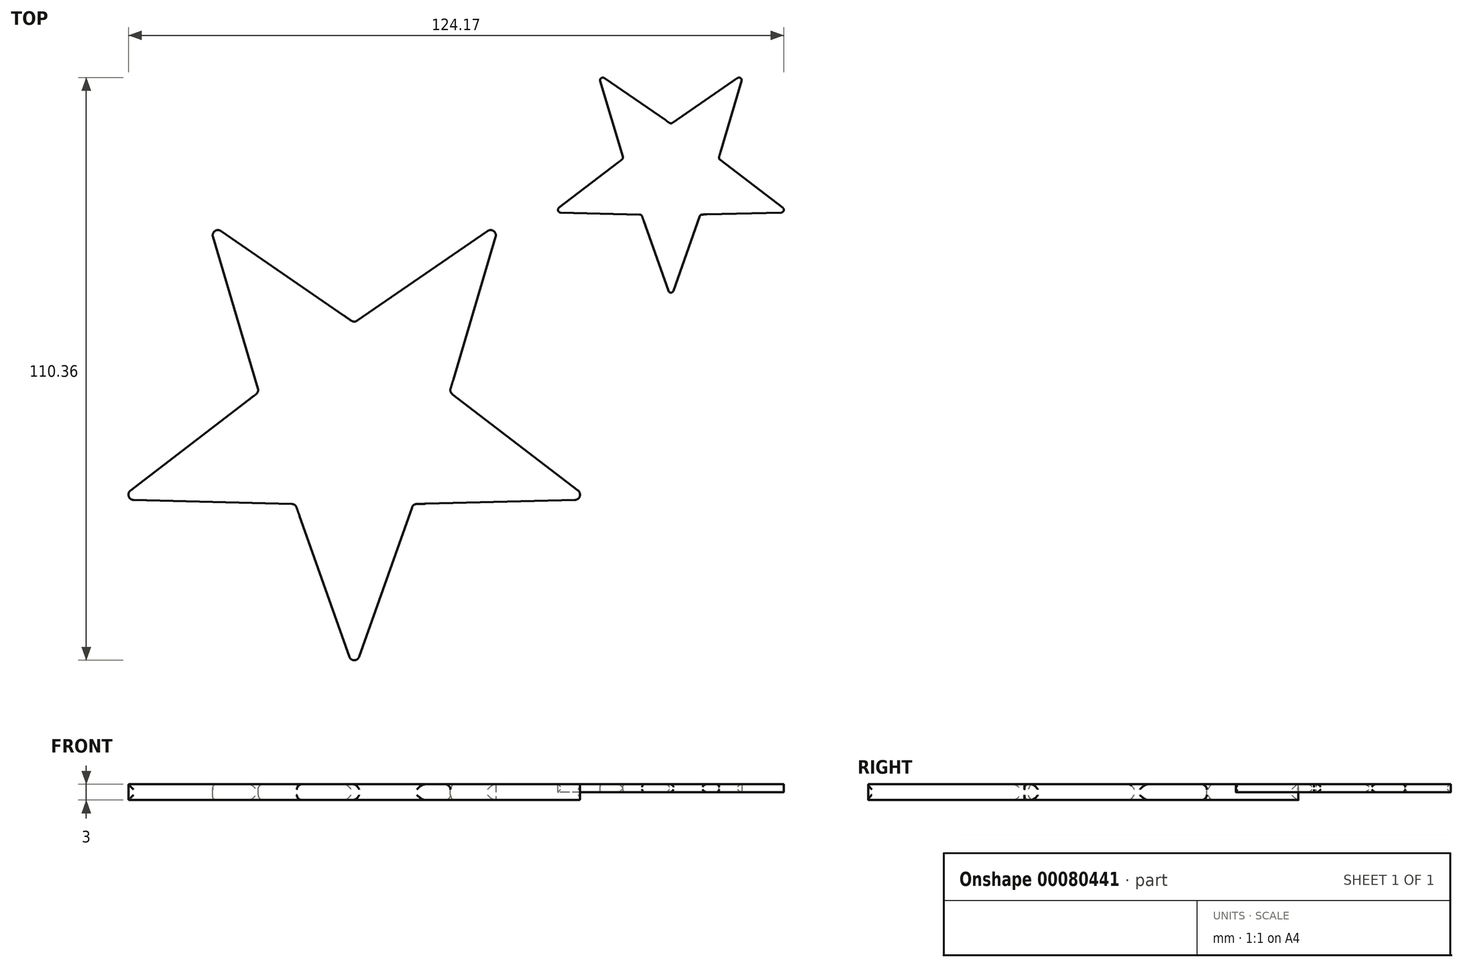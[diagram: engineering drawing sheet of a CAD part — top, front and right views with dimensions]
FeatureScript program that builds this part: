
annotation { "Feature Type Name" : "Feature", "Feature Type Description" : "" }
export const myFeature = defineFeature(function(context is Context, id is Id, definition is map)
    precondition{}
    {
        {
            var Q0;
            Q0=qCreatedBy(makeId("Top.planeOp"),FACE);
            var sketch = newSketch(context, id + "F0", { "sketchPlane" : qUnion([Q0])});
            skPoint(sketch, "E0.0.midPoint", {"position": v(0, -30.72) * mm});
            skPoint(sketch, "E1.0.midPoint", {"position": v(22.32, -30.72) * mm});
            skLineSegment(sketch, "E2", {"start": v(-27.59, 37.97) * mm, "end": v(-18.06, 5.87) * mm});
            skLineSegment(sketch, "E3", {"start": v(-18.06, 5.87) * mm, "end": v(-44.64, -14.5) * mm});
            skLineSegment(sketch, "E4", {"start": v(-27.59, 37.97) * mm, "end": v(0, 18.99) * mm});
            skLineSegment(sketch, "E5", {"start": v(0, 18.99) * mm, "end": v(27.59, 37.97) * mm});
            skLineSegment(sketch, "E6", {"start": v(27.59, 37.97) * mm, "end": v(18.06, 5.87) * mm});
            skLineSegment(sketch, "E7", {"start": v(18.06, 5.87) * mm, "end": v(44.64, -14.5) * mm});
            skLineSegment(sketch, "E8", {"start": v(44.64, -14.5) * mm, "end": v(11.16, -15.36) * mm});
            skLineSegment(sketch, "E9", {"start": v(11.16, -15.36) * mm, "end": v(0, -46.94) * mm});
            skLineSegment(sketch, "E10", {"start": v(-11.16, -15.36) * mm, "end": v(-44.64, -14.5) * mm});
            skLineSegment(sketch, "E11", {"start": v(-11.16, -15.36) * mm, "end": v(0, -46.94) * mm});
            skSolve(sketch);
        }
        {
            var Q0;
            Q0 = qSketchRegion(id + "F0", true);
            extrude(context, id + "F1", {"entities" : qUnion([Q0]), "depth" : 3 * mm});
        }
        {
            var Q0;
            Q0=makeQuery(id+"F1.opExtrude","SWEPT_FACE",FACE,{"disambiguationData":[OSD([sQuery(id+"F0.wireOp",EDGE,"E10")])]});
            var Q1;
            Q1=makeQuery(id+"F1.opExtrude","SWEPT_FACE",FACE,{"disambiguationData":[OSD([sQuery(id+"F0.wireOp",EDGE,"E9")])]});
            var Q2;
            Q2=makeQuery(id+"F1.opExtrude","SWEPT_FACE",FACE,{"disambiguationData":[OSD([sQuery(id+"F0.wireOp",EDGE,"E7")])]});
            var Q3;
            Q3=makeQuery(id+"F1.opExtrude","SWEPT_FACE",FACE,{"disambiguationData":[OSD([sQuery(id+"F0.wireOp",EDGE,"E5")])]});
            var Q4;
            Q4=makeQuery(id+"F1.opExtrude","SWEPT_FACE",FACE,{"disambiguationData":[OSD([sQuery(id+"F0.wireOp",EDGE,"E2")])]});
            fillet(context, id + "F2", {"entities" : qUnion([Q0, Q1, Q2, Q3, Q4]), "radius" : 1 * mm, "tangentPropagation" : true, "allowEdgeOverflow" : false});
        }
        {
            var Q0;
            Q0=makeQuery(id+"F1.opExtrude","SWEPT_BODY",BODY,{"disambiguationData":[OSD([sQuery(id+"F0.wireOp",EDGE,"E2"),sQuery(id+"F0.wireOp",EDGE,"E3"),sQuery(id+"F0.wireOp",EDGE,"E4"),sQuery(id+"F0.wireOp",EDGE,"E5"),sQuery(id+"F0.wireOp",EDGE,"E6"),sQuery(id+"F0.wireOp",EDGE,"E7"),sQuery(id+"F0.wireOp",EDGE,"E8"),sQuery(id+"F0.wireOp",EDGE,"E9"),sQuery(id+"F0.wireOp",EDGE,"E10"),sQuery(id+"F0.wireOp",EDGE,"E11")])]});
            transform(context, id + "F3", {"entities" : qUnion([Q0]), "transformType" : TransformType.TRANSLATION_3D, "dx" : 55 * mm, "dy" : 55 * mm, "dz" : 0 * mm, "makeCopy" : true});
        }
        {
            var Q0;
            Q0=makeQuery(id+"F3.opPattern","COPY",BODY,{"derivedFrom":makeQuery(id+"F1.opExtrude","SWEPT_BODY",BODY,{"disambiguationData":[OSD([sQuery(id+"F0.wireOp",EDGE,"E2"),sQuery(id+"F0.wireOp",EDGE,"E3"),sQuery(id+"F0.wireOp",EDGE,"E4"),sQuery(id+"F0.wireOp",EDGE,"E5"),sQuery(id+"F0.wireOp",EDGE,"E6"),sQuery(id+"F0.wireOp",EDGE,"E7"),sQuery(id+"F0.wireOp",EDGE,"E8"),sQuery(id+"F0.wireOp",EDGE,"E9"),sQuery(id+"F0.wireOp",EDGE,"E10"),sQuery(id+"F0.wireOp",EDGE,"E11")])]}),"instanceName":"1"});
            var Q1;
            {var subQ0=sQuery(id+"F0.wireOp",EDGE,"E11");var subQ1=sQuery(id+"F0.wireOp",EDGE,"E9");Q1=makeQuery(id+"F3.opPattern","COPY",VERTEX,{"derivedFrom":makeQuery(id+"F2.opFillet","BLEND_VERTEX",VERTEX,{"blendedFrom":[makeQuery(id+"F1.opExtrude","CAP_VERTEX",VERTEX,{"disambiguationData":[OSD([subQ1,subQ0])],"isStart":false}),makeQuery(id+"F1.opExtrude","CAP_EDGE",EDGE,{"disambiguationData":[OSD([subQ1])],"isStart":false}),makeQuery(id+"F1.opExtrude","CAP_EDGE",EDGE,{"disambiguationData":[OSD([subQ0])],"isStart":false}),makeQuery(id+"F1.opExtrude","CAP_FACE",FACE,{"disambiguationData":[OSD([sQuery(id+"F0.wireOp",EDGE,"E2"),sQuery(id+"F0.wireOp",EDGE,"E3"),sQuery(id+"F0.wireOp",EDGE,"E4"),sQuery(id+"F0.wireOp",EDGE,"E5"),sQuery(id+"F0.wireOp",EDGE,"E6"),sQuery(id+"F0.wireOp",EDGE,"E7"),sQuery(id+"F0.wireOp",EDGE,"E8"),subQ1,sQuery(id+"F0.wireOp",EDGE,"E10"),subQ0])],"isStart":false})],"blendedInto":[makeQuery(id+"F1.opExtrude","CAP_FACE",FACE,{"disambiguationData":[OSD([sQuery(id+"F0.wireOp",EDGE,"E2"),sQuery(id+"F0.wireOp",EDGE,"E3"),sQuery(id+"F0.wireOp",EDGE,"E4"),sQuery(id+"F0.wireOp",EDGE,"E5"),sQuery(id+"F0.wireOp",EDGE,"E6"),sQuery(id+"F0.wireOp",EDGE,"E7"),sQuery(id+"F0.wireOp",EDGE,"E8"),subQ1,sQuery(id+"F0.wireOp",EDGE,"E10"),subQ0])],"isStart":false})]}),"instanceName":"1"});}
            transform(context, id + "F4", {"entities" : qUnion([Q0]), "transformType" : TransformType.SCALE_UNIFORMLY, "scale" : 0.5, "scalePoint" : qUnion([Q1]), "makeCopy" : false});
        }
    });
